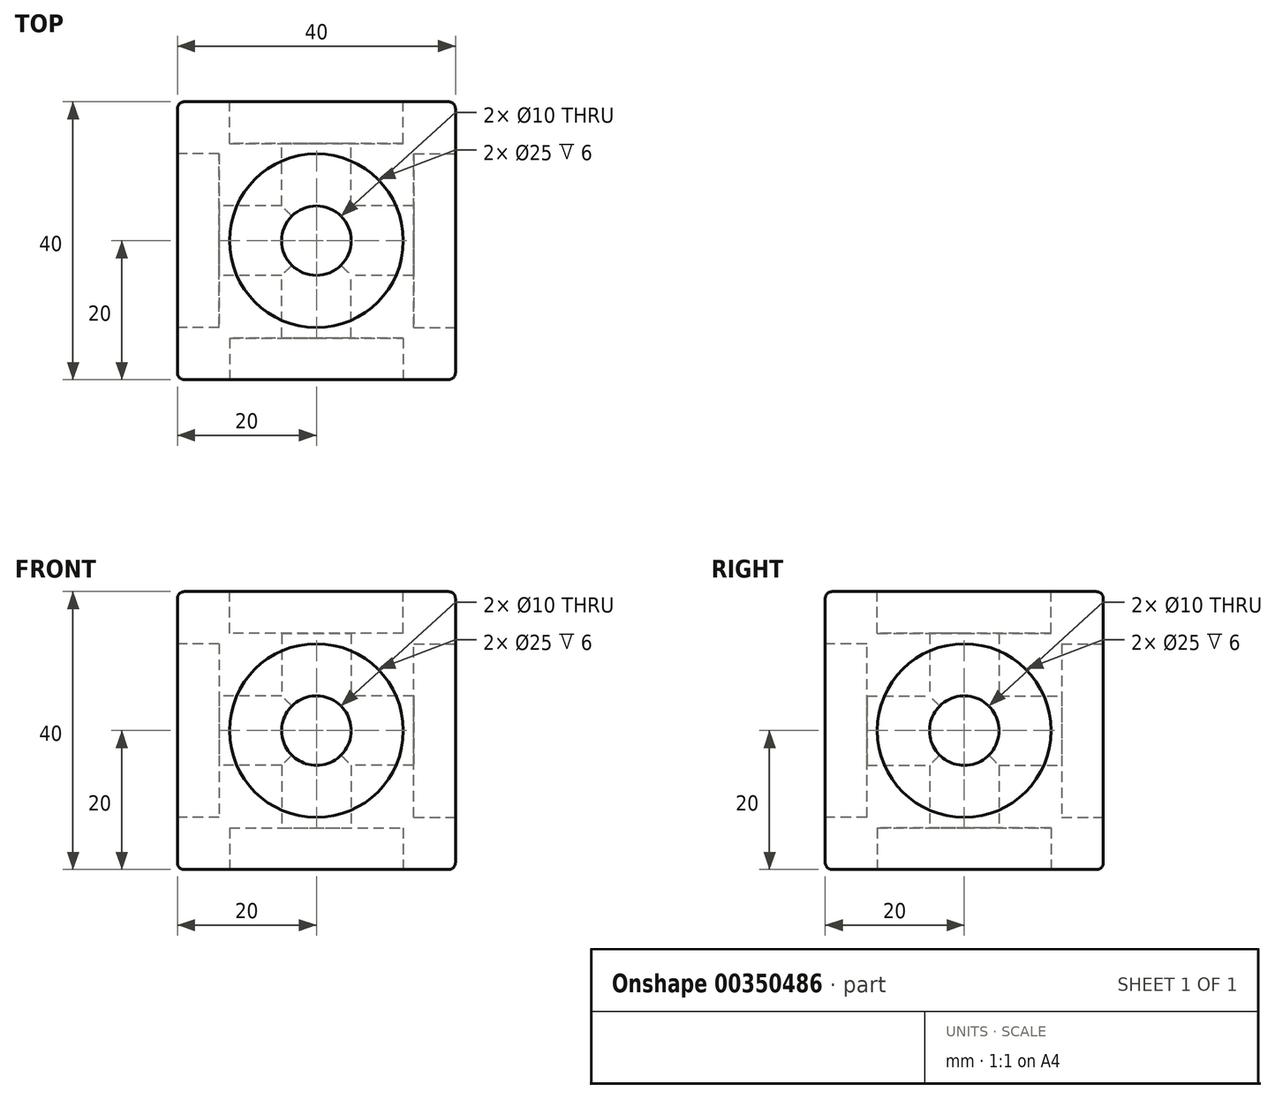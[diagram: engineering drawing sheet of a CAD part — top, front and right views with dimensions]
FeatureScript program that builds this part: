
annotation { "Feature Type Name" : "Feature", "Feature Type Description" : "" }
export const myFeature = defineFeature(function(context is Context, id is Id, definition is map)
    precondition{}
    {
        {
            var Q0;
            Q0=qCreatedBy(makeId("Top.planeOp"),FACE);
            var sketch = newSketch(context, id + "F0", { "sketchPlane" : qUnion([Q0])});
            skLineSegment(sketch, "E0.bottom", {"start": v(20, 20) * mm, "end": v(-20, 20) * mm});
            skLineSegment(sketch, "E0.top", {"start": v(20, -20) * mm, "end": v(-20, -20) * mm});
            skLineSegment(sketch, "E0.left", {"start": v(20, 20) * mm, "end": v(20, -20) * mm});
            skLineSegment(sketch, "E0.right", {"start": v(-20, 20) * mm, "end": v(-20, -20) * mm});
            skPoint(sketch, "E0.middle", {"position": v(0, 0) * mm});
            skCircle(sketch, "E1", {"center": v(0, 0) * mm, "radius": 5 * mm});
            skSolve(sketch);
        }
        {
            var Q0;
            Q0 = qSketchRegion(id + "F0", true);
            var Q1;
            Q1=makeQuery(id+"F0.imprint","IMPRINT",FACE,{"disambiguationData":[TD([[makeQuery(id+"F0.imprint","IMPRINT",EDGE,{"derivedFrom":sQuery(id+"F0.wireOp",EDGE,"E1")}),-1.0]])]});
            extrude(context, id + "F1", {"entities" : qUnion([Q0, Q1]), "endBound" : BoundingType.SYMMETRIC, "depth" : 40 * mm});
        }
        {
            var Q0;
            Q0=makeQuery(id+"F1.opExtrude","CAP_FACE",FACE,{"disambiguationData":[OSD([sQuery(id+"F0.wireOp",EDGE,"E0.bottom"),sQuery(id+"F0.wireOp",EDGE,"E0.top"),sQuery(id+"F0.wireOp",EDGE,"E0.left"),sQuery(id+"F0.wireOp",EDGE,"E0.right"),sQuery(id+"F0.wireOp",EDGE,"E1")])],"isStart":false});
            var sketch = newSketch(context, id + "F2", { "sketchPlane" : qUnion([Q0])});
            skCircle(sketch, "E2", {"center": v(0, 0) * mm, "radius": 12.5 * mm});
            skSolve(sketch);
        }
        {
            var Q0;
            Q0 = qSketchRegion(id + "F2", true);
            extrude(context, id + "F3", {"entities" : qUnion([Q0]), "operationType" : NewBodyOperationType.REMOVE, "oppositeDirection" : true, "depth" : 6 * mm});
        }
        {
            var Q0;
            Q0=makeQuery(id+"F1.opExtrude","CAP_FACE",FACE,{"disambiguationData":[OSD([sQuery(id+"F0.wireOp",EDGE,"E0.bottom"),sQuery(id+"F0.wireOp",EDGE,"E0.top"),sQuery(id+"F0.wireOp",EDGE,"E0.left"),sQuery(id+"F0.wireOp",EDGE,"E0.right"),sQuery(id+"F0.wireOp",EDGE,"E1")])],"isStart":true});
            var sketch = newSketch(context, id + "F4", { "sketchPlane" : qUnion([Q0])});
            skCircle(sketch, "E3", {"center": v(0, 0) * mm, "radius": 12.5 * mm});
            skSolve(sketch);
        }
        {
            var Q0;
            Q0 = qSketchRegion(id + "F4", true);
            extrude(context, id + "F5", {"entities" : qUnion([Q0]), "operationType" : NewBodyOperationType.REMOVE, "oppositeDirection" : true, "depth" : 6 * mm});
        }
        {
            var Q0;
            Q0=makeQuery(id+"F1.opExtrude","SWEPT_FACE",FACE,{"disambiguationData":[OSD([sQuery(id+"F0.wireOp",EDGE,"E0.top")])]});
            var sketch = newSketch(context, id + "F6", { "sketchPlane" : qUnion([Q0])});
            skCircle(sketch, "E4", {"center": v(0, 0) * mm, "radius": 12.5 * mm});
            skSolve(sketch);
        }
        {
            var Q0;
            Q0 = qSketchRegion(id + "F6", true);
            extrude(context, id + "F7", {"entities" : qUnion([Q0]), "operationType" : NewBodyOperationType.REMOVE, "oppositeDirection" : true, "depth" : 6 * mm});
        }
        {
            var Q0;
            Q0=qCreatedBy(makeId("Front.planeOp"),FACE);
            var sketch = newSketch(context, id + "F8", { "sketchPlane" : qUnion([Q0])});
            skCircle(sketch, "E5", {"center": v(0, 0) * mm, "radius": 5 * mm});
            skSolve(sketch);
        }
        {
            var Q0;
            Q0 = qSketchRegion(id + "F8", true);
            extrude(context, id + "F9", {"entities" : qUnion([Q0]), "operationType" : NewBodyOperationType.REMOVE, "endBound" : BoundingType.SYMMETRIC, "depth" : 40 * mm});
        }
        {
            var Q0;
            Q0=qCreatedBy(makeId("Right.planeOp"),FACE);
            var sketch = newSketch(context, id + "F10", { "sketchPlane" : qUnion([Q0])});
            skCircle(sketch, "E6", {"center": v(0, 0) * mm, "radius": 5 * mm});
            skSolve(sketch);
        }
        {
            var Q0;
            Q0 = qSketchRegion(id + "F10", true);
            extrude(context, id + "F11", {"entities" : qUnion([Q0]), "operationType" : NewBodyOperationType.REMOVE, "endBound" : BoundingType.SYMMETRIC, "depth" : 40 * mm});
        }
        {
            var Q0;
            Q0=makeQuery(id+"F1.opExtrude","SWEPT_FACE",FACE,{"disambiguationData":[OSD([sQuery(id+"F0.wireOp",EDGE,"E0.left")])]});
            var sketch = newSketch(context, id + "F12", { "sketchPlane" : qUnion([Q0])});
            skCircle(sketch, "E7", {"center": v(0, 0) * mm, "radius": 12.5 * mm});
            skSolve(sketch);
        }
        {
            var Q0;
            Q0 = qSketchRegion(id + "F12", true);
            extrude(context, id + "F13", {"entities" : qUnion([Q0]), "operationType" : NewBodyOperationType.REMOVE, "oppositeDirection" : true, "depth" : 6 * mm});
        }
        {
            var Q0;
            Q0=makeQuery(id+"F1.opExtrude","SWEPT_FACE",FACE,{"disambiguationData":[OSD([sQuery(id+"F0.wireOp",EDGE,"E0.bottom")])]});
            var sketch = newSketch(context, id + "F14", { "sketchPlane" : qUnion([Q0])});
            skCircle(sketch, "E8", {"center": v(0, 0) * mm, "radius": 12.5 * mm});
            skSolve(sketch);
        }
        {
            var Q0;
            Q0 = qSketchRegion(id + "F14", true);
            extrude(context, id + "F15", {"entities" : qUnion([Q0]), "operationType" : NewBodyOperationType.REMOVE, "oppositeDirection" : true, "depth" : 6 * mm});
        }
        {
            var Q0;
            Q0=makeQuery(id+"F1.opExtrude","SWEPT_FACE",FACE,{"disambiguationData":[OSD([sQuery(id+"F0.wireOp",EDGE,"E0.right")])]});
            var sketch = newSketch(context, id + "F16", { "sketchPlane" : qUnion([Q0])});
            skCircle(sketch, "E9", {"center": v(0, 0) * mm, "radius": 12.5 * mm});
            skSolve(sketch);
        }
        {
            var Q0;
            Q0 = qSketchRegion(id + "F16", true);
            extrude(context, id + "F17", {"entities" : qUnion([Q0]), "operationType" : NewBodyOperationType.REMOVE, "oppositeDirection" : true, "depth" : 6 * mm});
        }
        {
            var Q0;
            Q0=makeQuery(id+"F1.opExtrude","SWEPT_EDGE",EDGE,{"disambiguationData":[OSD([sQuery(id+"F0.wireOp",EDGE,"E0.top"),sQuery(id+"F0.wireOp",EDGE,"E0.right")])]});
            var Q1;
            Q1=makeQuery(id+"F1.opExtrude","CAP_EDGE",EDGE,{"disambiguationData":[OSD([sQuery(id+"F0.wireOp",EDGE,"E0.right")])],"isStart":true});
            var Q2;
            Q2=makeQuery(id+"F1.opExtrude","CAP_EDGE",EDGE,{"disambiguationData":[OSD([sQuery(id+"F0.wireOp",EDGE,"E0.top")])],"isStart":true});
            var Q3;
            Q3=makeQuery(id+"F1.opExtrude","SWEPT_EDGE",EDGE,{"disambiguationData":[OSD([sQuery(id+"F0.wireOp",EDGE,"E0.top"),sQuery(id+"F0.wireOp",EDGE,"E0.left")])]});
            var Q4;
            Q4=makeQuery(id+"F1.opExtrude","CAP_EDGE",EDGE,{"disambiguationData":[OSD([sQuery(id+"F0.wireOp",EDGE,"E0.top")])],"isStart":false});
            var Q5;
            Q5=makeQuery(id+"F1.opExtrude","CAP_EDGE",EDGE,{"disambiguationData":[OSD([sQuery(id+"F0.wireOp",EDGE,"E0.right")])],"isStart":false});
            var Q6;
            Q6=makeQuery(id+"F1.opExtrude","SWEPT_EDGE",EDGE,{"disambiguationData":[OSD([sQuery(id+"F0.wireOp",EDGE,"E0.bottom"),sQuery(id+"F0.wireOp",EDGE,"E0.right")])]});
            var Q7;
            Q7=makeQuery(id+"F1.opExtrude","CAP_EDGE",EDGE,{"disambiguationData":[OSD([sQuery(id+"F0.wireOp",EDGE,"E0.bottom")])],"isStart":true});
            var Q8;
            Q8=makeQuery(id+"F1.opExtrude","CAP_EDGE",EDGE,{"disambiguationData":[OSD([sQuery(id+"F0.wireOp",EDGE,"E0.left")])],"isStart":true});
            var Q9;
            Q9=makeQuery(id+"F1.opExtrude","CAP_EDGE",EDGE,{"disambiguationData":[OSD([sQuery(id+"F0.wireOp",EDGE,"E0.left")])],"isStart":false});
            var Q10;
            Q10=makeQuery(id+"F1.opExtrude","CAP_EDGE",EDGE,{"disambiguationData":[OSD([sQuery(id+"F0.wireOp",EDGE,"E0.bottom")])],"isStart":false});
            var Q11;
            Q11=makeQuery(id+"F1.opExtrude","SWEPT_EDGE",EDGE,{"disambiguationData":[OSD([sQuery(id+"F0.wireOp",EDGE,"E0.bottom"),sQuery(id+"F0.wireOp",EDGE,"E0.left")])]});
            fillet(context, id + "F18", {"entities" : qUnion([Q0, Q1, Q2, Q3, Q4, Q5, Q6, Q7, Q8, Q9, Q10, Q11]), "radius" : 1 * mm, "tangentPropagation" : true, "allowEdgeOverflow" : false});
        }
    });
